# Revit family: L-trade 55 Standart Easy Lock
name_source: partatom
category: Осветительные приборы
revit_build: Autodesk Revit 2017 (Build: 20160225_1515(x64)
units: mm (PartAtom-declared; Revit-internal decimal feet)

## family parameters
Источник света = Да
Общий = Нет
Основа = Грань
При загрузке вырезать с полостями = Нет
Размер круглого соединителя = Использовать диаметр
Тип детали = Нормальный
Точка расчета площади = Нет

## types (8) — shared parameters
Видимая форма излучения при визуализации = Нет
Длина профиля = 1000 мм
Излучение по длине прямоугольника = 985 мм
Излучение по ширине прямоугольника = 38 мм
Классификация нагрузок = Освещение
Комментарии к типоразмеру = Торговые
Описание = Светодиодный светильник L-trade 55 Standart предназначен для освещения промышленных помещений, логистических центров, магазинов, спортивных сооружений и т.д.
Отметка по умолчанию = 1219 мм
Полная установленная мощность = 52 В·А
Расстояние от светильника до поверхности = 100 мм
Световой поток светильника = 4517 лм
Светофильтр = 16777215
Смещение цветовой температуры при затухании лампы = <Нет>
Угол наклона = 90.00°

## per-type parameters (varying)
| type | Артикул | Изготовитель | Кривая сил света | Файл фотометрической сетки | Цветовая температура |
| L-trade 55 Standart Easy Lock 4.0K Д | 313204500842100 |  | Д | L-trade 55-45-D-4.0K-02-Standart.ies | 4000 K |
| L-trade 55 Standart Easy Lock 5.0K Д | 231011 |  | Д | L-trade 55-45-Д-5.0K-02-Standart.ies | 5000 K |
| L-trade 55 Standart Easy Lock 4.0K К15 |  |  | К15 | L-trade 55-52-K15-4.0K-01-Standart.ies | 4000 K |
| L-trade 55 Standart Easy Lock 4.0K Г30 |  |  | Г30 | L-trade 55-52-G30-4.0K-01-Standart.ies | 4000 K |
| L-trade 55 Standart Easy Lock 4.0K Г60 |  |  | Г60 | L-trade 55-52-G60-4.0K-01-Standart.ies | 4000 K |
| L-trade 55 Standart Easy Lock 5.0K К15 |  | LEDEL | К15 | L-trade 55-52-K15-5.0K-01-Standart.ies | 5000 K |
| L-trade 55 Standart Easy Lock 5.0K Г30 |  |  | Г30 | L-trade 55-52-G30-5.0K-01-Standart.ies | 5000 K |
| L-trade 55 Standart Easy Lock 5.0K Г60 |  |  | Г60 | L-trade 55-45-D-5.0K-02-Standart.ies | 5000 K |

## geometry (parser evidence)
native form markers: Sweep x5
no freeform markers — native parametric forms only
